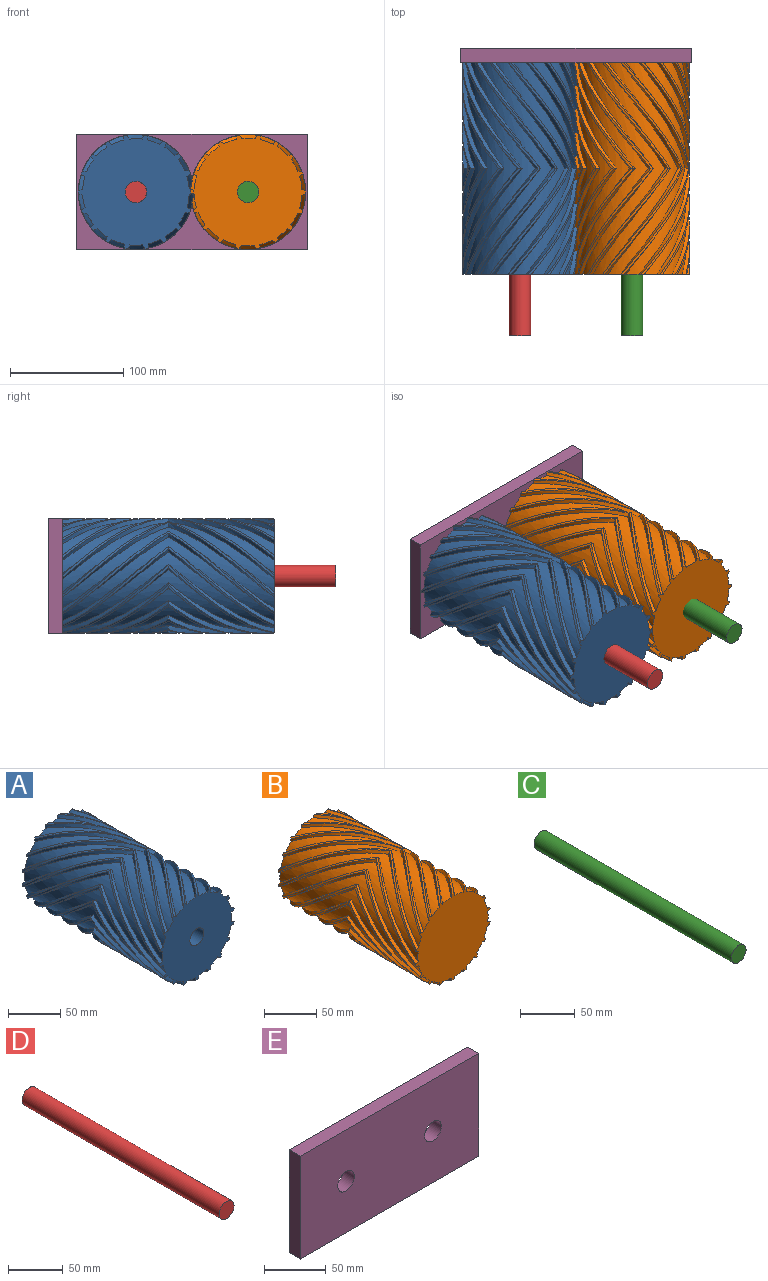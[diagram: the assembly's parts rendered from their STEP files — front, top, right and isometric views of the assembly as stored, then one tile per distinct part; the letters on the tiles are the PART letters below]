
ASSEMBLY  parts=5 mates=3
PART A: 129 faces, bbox 102.5x186.9x102.5 mm
  f0: plane 101.65x100.54mm, normal (0,-1,0), area 6946.6mm2, adj f1,f2,f3,f4,f5,f6,f7,f8
  f1: bspline ~93.47x69.89mm, area 471mm2, adj f0,f2,f4,f23
  f2: bspline ~93.47x71.15mm, area 235.9mm2, adj f0,f1,f3,f24
  f3: bspline ~93.47x68.96mm, area 471mm2, adj f0,f2,f16,f25
  f4: cylinder r=47.1mm len=186.94mm, axis (0,1,0), area 2157.7mm2, adj f0,f1,f22,f23,f97,f100
  f5: cylinder r=47.1mm len=186.94mm, axis (0,1,0), area 2157.7mm2, adj f0,f22,f31,f34,f35,f38
  f6: cylinder r=47.1mm len=186.94mm, axis (0,1,0), area 2157.7mm2, adj f0,f22,f37,f40,f41,f44
  f7: cylinder r=47.1mm len=186.94mm, axis (0,1,0), area 2157.7mm2, adj f0,f22,f43,f46,f47,f50
  f8: cylinder r=47.1mm len=186.94mm, axis (0,1,0), area 2157.7mm2, adj f0,f22,f49,f52,f53,f56
  f9: cylinder r=47.1mm len=186.94mm, axis (0,1,0), area 2157.7mm2, adj f0,f22,f55,f58,f59,f62
  f10: cylinder r=47.1mm len=186.94mm, axis (0,1,0), area 2157.7mm2, adj f0,f22,f61,f64,f65,f68
  f11: cylinder r=47.1mm len=186.94mm, axis (0,1,0), area 2157.7mm2, adj f0,f22,f67,f70,f77,f80
  f12: cylinder r=47.1mm len=186.94mm, axis (0,1,0), area 2157.7mm2, adj f0,f22,f73,f76,f89,f92
  f13: cylinder r=47.1mm len=186.94mm, axis (0,1,0), area 2157.7mm2, adj f0,f22,f71,f74,f79,f82
  f14: cylinder r=47.1mm len=186.94mm, axis (0,1,0), area 2157.7mm2, adj f0,f22,f85,f88,f95,f98
  f15: cylinder r=47.1mm len=186.94mm, axis (0,1,0), area 2157.7mm2, adj f0,f22,f83,f86,f91,f94
  f16: cylinder r=47.1mm len=186.94mm, axis (0,1,0), area 2157.7mm2, adj f0,f3,f22,f25,f26,f125
  f17: cylinder r=47.1mm len=186.94mm, axis (0,1,0), area 2157.7mm2, adj f0,f22,f103,f106,f113,f116
  f18: cylinder r=47.1mm len=186.94mm, axis (0,1,0), area 2157.7mm2, adj f0,f22,f29,f32,f109,f112
  f19: cylinder r=47.1mm len=186.94mm, axis (0,1,0), area 2157.7mm2, adj f0,f22,f115,f118,f119,f122
  f20: cylinder r=47.1mm len=186.94mm, axis (0,1,0), area 2157.7mm2, adj f0,f22,f107,f110,f121,f124
  f21: cylinder r=47.1mm len=186.94mm, axis (0,1,0), area 2157.7mm2, adj f0,f22,f28,f101,f104,f127
  f22: plane 101.65x100.54mm, normal (0,1,0), area 6946.6mm2, adj f4,f5,f6,f7,f8,f9,f10,f11
  f23: bspline ~93.47x69.89mm, area 471mm2, adj f1,f4,f22,f24
  f24: bspline ~93.47x71.15mm, area 235.9mm2, adj f2,f22,f23,f25
  f25: bspline ~93.47x68.96mm, area 471mm2, adj f3,f16,f22,f24
  f26: bspline ~93.47x60.41mm, area 471mm2, adj f16,f22,f27,f125
  f27: bspline ~93.47x60.34mm, area 235.9mm2, adj f22,f26,f28,f126
  f28: bspline ~93.47x57.85mm, area 471mm2, adj f21,f22,f27,f127
  f29: bspline ~93.47x53.27mm, area 471mm2, adj f18,f22,f30,f32
  f30: bspline ~93.47x52.25mm, area 235.9mm2, adj f22,f29,f31,f33
  f31: bspline ~93.47x53.27mm, area 471mm2, adj f5,f22,f30,f34
  f32: bspline ~93.47x53.27mm, area 471mm2, adj f0,f18,f29,f33
  f33: bspline ~93.47x52.25mm, area 235.9mm2, adj f0,f30,f32,f34
  f34: bspline ~93.47x53.27mm, area 471mm2, adj f0,f5,f31,f33
  f35: bspline ~93.47x64.39mm, area 471mm2, adj f0,f5,f36,f38
  f36: bspline ~93.47x66.76mm, area 235.9mm2, adj f0,f35,f37,f39
  f37: bspline ~93.47x66.03mm, area 471mm2, adj f0,f6,f36,f40
  f38: bspline ~93.47x64.39mm, area 471mm2, adj f5,f22,f35,f39
  f39: bspline ~93.47x66.76mm, area 235.9mm2, adj f22,f36,f38,f40
  f40: bspline ~93.47x66.03mm, area 471mm2, adj f6,f22,f37,f39
  f41: bspline ~93.47x71.45mm, area 471mm2, adj f0,f6,f42,f44
  f42: bspline ~93.47x73.38mm, area 235.9mm2, adj f0,f41,f43,f45
  f43: bspline ~93.47x71.76mm, area 471mm2, adj f0,f7,f42,f46
  f44: bspline ~93.47x71.45mm, area 471mm2, adj f6,f22,f41,f45
  f45: bspline ~93.47x73.38mm, area 235.9mm2, adj f22,f42,f44,f46
  f46: bspline ~93.47x71.76mm, area 471mm2, adj f7,f22,f43,f45
  f47: bspline ~93.47x69.89mm, area 471mm2, adj f0,f7,f48,f50
  f48: bspline ~93.47x71.15mm, area 235.9mm2, adj f0,f47,f49,f51
  f49: bspline ~93.47x68.96mm, area 471mm2, adj f0,f8,f48,f52
  f50: bspline ~93.47x69.89mm, area 471mm2, adj f7,f22,f47,f51
  f51: bspline ~93.47x71.15mm, area 235.9mm2, adj f22,f48,f50,f52
  f52: bspline ~93.47x68.96mm, area 471mm2, adj f8,f22,f49,f51
  f53: bspline ~93.47x60.41mm, area 471mm2, adj f0,f8,f54,f56
  f54: bspline ~93.47x60.34mm, area 235.9mm2, adj f0,f53,f55,f57
  f55: bspline ~93.47x57.85mm, area 471mm2, adj f0,f9,f54,f58
  f56: bspline ~93.47x60.41mm, area 471mm2, adj f8,f22,f53,f57
  f57: bspline ~93.47x60.34mm, area 235.9mm2, adj f22,f54,f56,f58
  f58: bspline ~93.47x57.85mm, area 471mm2, adj f9,f22,f55,f57
  f59: bspline ~93.47x57.85mm, area 471mm2, adj f0,f9,f60,f62
  f60: bspline ~93.47x60.34mm, area 235.9mm2, adj f0,f59,f61,f63
  f61: bspline ~93.47x60.41mm, area 471mm2, adj f0,f10,f60,f64
  f62: bspline ~93.47x57.85mm, area 471mm2, adj f9,f22,f59,f63
  f63: bspline ~93.47x60.34mm, area 235.9mm2, adj f22,f60,f62,f64
  f64: bspline ~93.47x60.41mm, area 471mm2, adj f10,f22,f61,f63
  f65: bspline ~93.47x68.96mm, area 471mm2, adj f0,f10,f66,f68
  f66: bspline ~93.47x71.15mm, area 235.9mm2, adj f0,f65,f67,f69
  f67: bspline ~93.47x69.89mm, area 471mm2, adj f0,f11,f66,f70
  f68: bspline ~93.47x68.96mm, area 471mm2, adj f10,f22,f65,f69
  f69: bspline ~93.47x71.15mm, area 235.9mm2, adj f22,f66,f68,f70
  f70: bspline ~93.47x69.89mm, area 471mm2, adj f11,f22,f67,f69
  f71: bspline ~93.47x66.03mm, area 471mm2, adj f0,f13,f72,f74
  f72: bspline ~93.47x66.76mm, area 235.9mm2, adj f0,f71,f73,f75
  f73: bspline ~93.47x64.39mm, area 471mm2, adj f0,f12,f72,f76
  f74: bspline ~93.47x66.03mm, area 471mm2, adj f13,f22,f71,f75
  f75: bspline ~93.47x66.76mm, area 235.9mm2, adj f22,f72,f74,f76
  f76: bspline ~93.47x64.39mm, area 471mm2, adj f12,f22,f73,f75
  f77: bspline ~93.47x71.76mm, area 471mm2, adj f0,f11,f78,f80
  f78: bspline ~93.47x73.38mm, area 235.9mm2, adj f0,f77,f79,f81
  f79: bspline ~93.47x71.45mm, area 471mm2, adj f0,f13,f78,f82
  f80: bspline ~93.47x71.76mm, area 471mm2, adj f11,f22,f77,f81
  f81: bspline ~93.47x73.38mm, area 235.9mm2, adj f22,f78,f80,f82
  f82: bspline ~93.47x71.45mm, area 471mm2, adj f13,f22,f79,f81
  f83: bspline ~93.47x64.39mm, area 471mm2, adj f0,f15,f84,f86
  f84: bspline ~93.47x66.76mm, area 235.9mm2, adj f0,f83,f85,f87
  f85: bspline ~93.47x66.03mm, area 471mm2, adj f0,f14,f84,f88
  f86: bspline ~93.47x64.39mm, area 471mm2, adj f15,f22,f83,f87
  f87: bspline ~93.47x66.76mm, area 235.9mm2, adj f22,f84,f86,f88
  f88: bspline ~93.47x66.03mm, area 471mm2, adj f14,f22,f85,f87
  f89: bspline ~93.47x53.27mm, area 471mm2, adj f0,f12,f90,f92
  f90: bspline ~93.47x52.25mm, area 235.9mm2, adj f0,f89,f91,f93
  f91: bspline ~93.47x53.27mm, area 471mm2, adj f0,f15,f90,f94
  f92: bspline ~93.47x53.27mm, area 471mm2, adj f12,f22,f89,f93
  f93: bspline ~93.47x52.25mm, area 235.9mm2, adj f22,f90,f92,f94
  f94: bspline ~93.47x53.27mm, area 471mm2, adj f15,f22,f91,f93
  f95: bspline ~93.47x71.45mm, area 471mm2, adj f0,f14,f96,f98
  f96: bspline ~93.47x73.38mm, area 235.9mm2, adj f0,f95,f97,f99
  f97: bspline ~93.47x71.76mm, area 471mm2, adj f0,f4,f96,f100
  f98: bspline ~93.47x71.45mm, area 471mm2, adj f14,f22,f95,f99
  f99: bspline ~93.47x73.38mm, area 235.9mm2, adj f22,f96,f98,f100
  f100: bspline ~93.47x71.76mm, area 471mm2, adj f4,f22,f97,f99
  f101: bspline ~93.47x57.85mm, area 471mm2, adj f21,f22,f102,f104
  f102: bspline ~93.47x60.34mm, area 235.9mm2, adj f22,f101,f103,f105
  f103: bspline ~93.47x60.41mm, area 471mm2, adj f17,f22,f102,f106
  f104: bspline ~93.47x57.85mm, area 471mm2, adj f0,f21,f101,f105
  f105: bspline ~93.47x60.34mm, area 235.9mm2, adj f0,f102,f104,f106
  f106: bspline ~93.47x60.41mm, area 471mm2, adj f0,f17,f103,f105
  f107: bspline ~93.47x66.03mm, area 471mm2, adj f20,f22,f108,f110
  f108: bspline ~93.47x66.76mm, area 235.9mm2, adj f22,f107,f109,f111
  f109: bspline ~93.47x64.39mm, area 471mm2, adj f18,f22,f108,f112
  f110: bspline ~93.47x66.03mm, area 471mm2, adj f0,f20,f107,f111
  f111: bspline ~93.47x66.76mm, area 235.9mm2, adj f0,f108,f110,f112
  f112: bspline ~93.47x64.39mm, area 471mm2, adj f0,f18,f109,f111
  f113: bspline ~93.47x68.96mm, area 471mm2, adj f17,f22,f114,f116
  f114: bspline ~93.47x71.15mm, area 235.9mm2, adj f22,f113,f115,f117
  f115: bspline ~93.47x69.89mm, area 471mm2, adj f19,f22,f114,f118
  f116: bspline ~93.47x68.96mm, area 471mm2, adj f0,f17,f113,f117
  f117: bspline ~93.47x71.15mm, area 235.9mm2, adj f0,f114,f116,f118
  f118: bspline ~93.47x69.89mm, area 471mm2, adj f0,f19,f115,f117
  f119: bspline ~93.47x71.76mm, area 471mm2, adj f19,f22,f120,f122
  f120: bspline ~93.47x73.38mm, area 235.9mm2, adj f22,f119,f121,f123
  f121: bspline ~93.47x71.45mm, area 471mm2, adj f20,f22,f120,f124
  f122: bspline ~93.47x71.76mm, area 471mm2, adj f0,f19,f119,f123
  f123: bspline ~93.47x73.38mm, area 235.9mm2, adj f0,f120,f122,f124
  f124: bspline ~93.47x71.45mm, area 471mm2, adj f0,f20,f121,f123
  f125: bspline ~93.47x60.41mm, area 471mm2, adj f0,f16,f26,f126
  f126: bspline ~93.47x60.34mm, area 235.9mm2, adj f0,f27,f125,f127
  f127: bspline ~93.47x57.85mm, area 471mm2, adj f0,f21,f28,f126
  f128: cylinder r=9.53mm len=186.94mm, axis (0,1,0), area 11188.1mm2, adj f0,f22
PART B: 128 faces, bbox 102.5x186.9x102.5 mm
  f0: plane 101.65x100.54mm, normal (0,-1,0), area 7343.5mm2, adj f1,f2,f3,f4,f5,f6,f7,f8
  f1: bspline ~93.47x69.89mm, area 406.7mm2, adj f0,f2,f4,f23
  f2: bspline ~93.47x71.15mm, area 235.9mm2, adj f0,f1,f3,f24
  f3: bspline ~93.47x68.96mm, area 406.7mm2, adj f0,f2,f16,f25
  f4: cylinder r=47.62mm len=186.94mm, axis (0,1,0), area 2227.2mm2, adj f0,f1,f22,f23,f97,f100
  f5: cylinder r=47.62mm len=186.94mm, axis (0,1,0), area 2227.2mm2, adj f0,f22,f31,f34,f35,f38
  f6: cylinder r=47.62mm len=186.94mm, axis (0,1,0), area 2227.2mm2, adj f0,f22,f37,f40,f41,f44
  f7: cylinder r=47.62mm len=186.94mm, axis (0,1,0), area 2227.2mm2, adj f0,f22,f43,f46,f47,f50
  f8: cylinder r=47.62mm len=186.94mm, axis (0,1,0), area 2227.2mm2, adj f0,f22,f49,f52,f53,f56
  f9: cylinder r=47.62mm len=186.94mm, axis (0,1,0), area 2227.2mm2, adj f0,f22,f55,f58,f59,f62
  f10: cylinder r=47.62mm len=186.94mm, axis (0,1,0), area 2227.2mm2, adj f0,f22,f61,f64,f65,f68
  f11: cylinder r=47.62mm len=186.94mm, axis (0,1,0), area 2227.2mm2, adj f0,f22,f67,f70,f77,f80
  f12: cylinder r=47.62mm len=186.94mm, axis (0,1,0), area 2227.2mm2, adj f0,f22,f73,f76,f89,f92
  f13: cylinder r=47.62mm len=186.94mm, axis (0,1,0), area 2227.2mm2, adj f0,f22,f71,f74,f79,f82
  f14: cylinder r=47.62mm len=186.94mm, axis (0,1,0), area 2227.2mm2, adj f0,f22,f85,f88,f95,f98
  f15: cylinder r=47.62mm len=186.94mm, axis (0,1,0), area 2227.2mm2, adj f0,f22,f83,f86,f91,f94
  f16: cylinder r=47.62mm len=186.94mm, axis (0,1,0), area 2227.2mm2, adj f0,f3,f22,f25,f26,f125
  f17: cylinder r=47.62mm len=186.94mm, axis (0,1,0), area 2227.2mm2, adj f0,f22,f103,f106,f113,f116
  f18: cylinder r=47.62mm len=186.94mm, axis (0,1,0), area 2227.2mm2, adj f0,f22,f29,f32,f109,f112
  f19: cylinder r=47.62mm len=186.94mm, axis (0,1,0), area 2227.2mm2, adj f0,f22,f115,f118,f119,f122
  f20: cylinder r=47.62mm len=186.94mm, axis (0,1,0), area 2227.2mm2, adj f0,f22,f107,f110,f121,f124
  f21: cylinder r=47.62mm len=186.94mm, axis (0,1,0), area 2227.2mm2, adj f0,f22,f28,f101,f104,f127
  f22: plane 101.65x100.54mm, normal (0,1,0), area 7343.5mm2, adj f4,f5,f6,f7,f8,f9,f10,f11
  f23: bspline ~93.47x69.89mm, area 406.7mm2, adj f1,f4,f22,f24
  f24: bspline ~93.47x71.15mm, area 235.9mm2, adj f2,f22,f23,f25
  f25: bspline ~93.47x68.96mm, area 406.7mm2, adj f3,f16,f22,f24
  f26: bspline ~93.47x60.41mm, area 406.7mm2, adj f16,f22,f27,f125
  f27: bspline ~93.47x60.34mm, area 235.9mm2, adj f22,f26,f28,f126
  f28: bspline ~93.47x57.85mm, area 406.7mm2, adj f21,f22,f27,f127
  f29: bspline ~93.47x53.18mm, area 406.7mm2, adj f18,f22,f30,f32
  f30: bspline ~93.47x52.25mm, area 235.9mm2, adj f22,f29,f31,f33
  f31: bspline ~93.47x53.18mm, area 406.7mm2, adj f5,f22,f30,f34
  f32: bspline ~93.47x53.18mm, area 406.7mm2, adj f0,f18,f29,f33
  f33: bspline ~93.47x52.25mm, area 235.9mm2, adj f0,f30,f32,f34
  f34: bspline ~93.47x53.18mm, area 406.7mm2, adj f0,f5,f31,f33
  f35: bspline ~93.47x64.39mm, area 406.7mm2, adj f0,f5,f36,f38
  f36: bspline ~93.47x66.76mm, area 235.9mm2, adj f0,f35,f37,f39
  f37: bspline ~93.47x66.02mm, area 406.7mm2, adj f0,f6,f36,f40
  f38: bspline ~93.47x64.39mm, area 406.7mm2, adj f5,f22,f35,f39
  f39: bspline ~93.47x66.76mm, area 235.9mm2, adj f22,f36,f38,f40
  f40: bspline ~93.47x66.02mm, area 406.7mm2, adj f6,f22,f37,f39
  f41: bspline ~93.47x71.45mm, area 406.7mm2, adj f0,f6,f42,f44
  f42: bspline ~93.47x73.38mm, area 235.9mm2, adj f0,f41,f43,f45
  f43: bspline ~93.47x71.76mm, area 406.7mm2, adj f0,f7,f42,f46
  f44: bspline ~93.47x71.45mm, area 406.7mm2, adj f6,f22,f41,f45
  f45: bspline ~93.47x73.38mm, area 235.9mm2, adj f22,f42,f44,f46
  f46: bspline ~93.47x71.76mm, area 406.7mm2, adj f7,f22,f43,f45
  f47: bspline ~93.47x69.89mm, area 406.7mm2, adj f0,f7,f48,f50
  f48: bspline ~93.47x71.15mm, area 235.9mm2, adj f0,f47,f49,f51
  f49: bspline ~93.47x68.96mm, area 406.7mm2, adj f0,f8,f48,f52
  f50: bspline ~93.47x69.89mm, area 406.7mm2, adj f7,f22,f47,f51
  f51: bspline ~93.47x71.15mm, area 235.9mm2, adj f22,f48,f50,f52
  f52: bspline ~93.47x68.96mm, area 406.7mm2, adj f8,f22,f49,f51
  f53: bspline ~93.47x60.41mm, area 406.7mm2, adj f0,f8,f54,f56
  f54: bspline ~93.47x60.34mm, area 235.9mm2, adj f0,f53,f55,f57
  f55: bspline ~93.47x57.85mm, area 406.7mm2, adj f0,f9,f54,f58
  f56: bspline ~93.47x60.41mm, area 406.7mm2, adj f8,f22,f53,f57
  f57: bspline ~93.47x60.34mm, area 235.9mm2, adj f22,f54,f56,f58
  f58: bspline ~93.47x57.85mm, area 406.7mm2, adj f9,f22,f55,f57
  f59: bspline ~93.47x57.85mm, area 406.7mm2, adj f0,f9,f60,f62
  f60: bspline ~93.47x60.34mm, area 235.9mm2, adj f0,f59,f61,f63
  f61: bspline ~93.47x60.41mm, area 406.7mm2, adj f0,f10,f60,f64
  f62: bspline ~93.47x57.85mm, area 406.7mm2, adj f9,f22,f59,f63
  f63: bspline ~93.47x60.34mm, area 235.9mm2, adj f22,f60,f62,f64
  f64: bspline ~93.47x60.41mm, area 406.7mm2, adj f10,f22,f61,f63
  f65: bspline ~93.47x68.96mm, area 406.7mm2, adj f0,f10,f66,f68
  f66: bspline ~93.47x71.15mm, area 235.9mm2, adj f0,f65,f67,f69
  f67: bspline ~93.47x69.89mm, area 406.7mm2, adj f0,f11,f66,f70
  f68: bspline ~93.47x68.96mm, area 406.7mm2, adj f10,f22,f65,f69
  f69: bspline ~93.47x71.15mm, area 235.9mm2, adj f22,f66,f68,f70
  f70: bspline ~93.47x69.89mm, area 406.7mm2, adj f11,f22,f67,f69
  f71: bspline ~93.47x66.02mm, area 406.7mm2, adj f0,f13,f72,f74
  f72: bspline ~93.47x66.76mm, area 235.9mm2, adj f0,f71,f73,f75
  f73: bspline ~93.47x64.39mm, area 406.7mm2, adj f0,f12,f72,f76
  f74: bspline ~93.47x66.02mm, area 406.7mm2, adj f13,f22,f71,f75
  f75: bspline ~93.47x66.76mm, area 235.9mm2, adj f22,f72,f74,f76
  f76: bspline ~93.47x64.39mm, area 406.7mm2, adj f12,f22,f73,f75
  f77: bspline ~93.47x71.76mm, area 406.7mm2, adj f0,f11,f78,f80
  f78: bspline ~93.47x73.38mm, area 235.9mm2, adj f0,f77,f79,f81
  f79: bspline ~93.47x71.45mm, area 406.7mm2, adj f0,f13,f78,f82
  f80: bspline ~93.47x71.76mm, area 406.7mm2, adj f11,f22,f77,f81
  f81: bspline ~93.47x73.38mm, area 235.9mm2, adj f22,f78,f80,f82
  f82: bspline ~93.47x71.45mm, area 406.7mm2, adj f13,f22,f79,f81
  f83: bspline ~93.47x64.39mm, area 406.7mm2, adj f0,f15,f84,f86
  f84: bspline ~93.47x66.76mm, area 235.9mm2, adj f0,f83,f85,f87
  f85: bspline ~93.47x66.02mm, area 406.7mm2, adj f0,f14,f84,f88
  f86: bspline ~93.47x64.39mm, area 406.7mm2, adj f15,f22,f83,f87
  f87: bspline ~93.47x66.76mm, area 235.9mm2, adj f22,f84,f86,f88
  f88: bspline ~93.47x66.02mm, area 406.7mm2, adj f14,f22,f85,f87
  f89: bspline ~93.47x53.18mm, area 406.7mm2, adj f0,f12,f90,f92
  f90: bspline ~93.47x52.25mm, area 235.9mm2, adj f0,f89,f91,f93
  f91: bspline ~93.47x53.18mm, area 406.7mm2, adj f0,f15,f90,f94
  f92: bspline ~93.47x53.18mm, area 406.7mm2, adj f12,f22,f89,f93
  f93: bspline ~93.47x52.25mm, area 235.9mm2, adj f22,f90,f92,f94
  f94: bspline ~93.47x53.18mm, area 406.7mm2, adj f15,f22,f91,f93
  f95: bspline ~93.47x71.45mm, area 406.7mm2, adj f0,f14,f96,f98
  f96: bspline ~93.47x73.38mm, area 235.9mm2, adj f0,f95,f97,f99
  f97: bspline ~93.47x71.76mm, area 406.7mm2, adj f0,f4,f96,f100
  f98: bspline ~93.47x71.45mm, area 406.7mm2, adj f14,f22,f95,f99
  f99: bspline ~93.47x73.38mm, area 235.9mm2, adj f22,f96,f98,f100
  f100: bspline ~93.47x71.76mm, area 406.7mm2, adj f4,f22,f97,f99
  f101: bspline ~93.47x57.85mm, area 406.7mm2, adj f21,f22,f102,f104
  f102: bspline ~93.47x60.34mm, area 235.9mm2, adj f22,f101,f103,f105
  f103: bspline ~93.47x60.41mm, area 406.7mm2, adj f17,f22,f102,f106
  f104: bspline ~93.47x57.85mm, area 406.7mm2, adj f0,f21,f101,f105
  f105: bspline ~93.47x60.34mm, area 235.9mm2, adj f0,f102,f104,f106
  f106: bspline ~93.47x60.41mm, area 406.7mm2, adj f0,f17,f103,f105
  f107: bspline ~93.47x66.02mm, area 406.7mm2, adj f20,f22,f108,f110
  f108: bspline ~93.47x66.76mm, area 235.9mm2, adj f22,f107,f109,f111
  f109: bspline ~93.47x64.39mm, area 406.7mm2, adj f18,f22,f108,f112
  f110: bspline ~93.47x66.02mm, area 406.7mm2, adj f0,f20,f107,f111
  f111: bspline ~93.47x66.76mm, area 235.9mm2, adj f0,f108,f110,f112
  f112: bspline ~93.47x64.39mm, area 406.7mm2, adj f0,f18,f109,f111
  f113: bspline ~93.47x68.96mm, area 406.7mm2, adj f17,f22,f114,f116
  f114: bspline ~93.47x71.15mm, area 235.9mm2, adj f22,f113,f115,f117
  f115: bspline ~93.47x69.89mm, area 406.7mm2, adj f19,f22,f114,f118
  f116: bspline ~93.47x68.96mm, area 406.7mm2, adj f0,f17,f113,f117
  f117: bspline ~93.47x71.15mm, area 235.9mm2, adj f0,f114,f116,f118
  f118: bspline ~93.47x69.89mm, area 406.7mm2, adj f0,f19,f115,f117
  f119: bspline ~93.47x71.76mm, area 406.7mm2, adj f19,f22,f120,f122
  f120: bspline ~93.47x73.38mm, area 235.9mm2, adj f22,f119,f121,f123
  f121: bspline ~93.47x71.45mm, area 406.7mm2, adj f20,f22,f120,f124
  f122: bspline ~93.47x71.76mm, area 406.7mm2, adj f0,f19,f119,f123
  f123: bspline ~93.47x73.38mm, area 235.9mm2, adj f0,f120,f122,f124
  f124: bspline ~93.47x71.45mm, area 406.7mm2, adj f0,f20,f121,f123
  f125: bspline ~93.47x60.41mm, area 406.7mm2, adj f0,f16,f26,f126
  f126: bspline ~93.47x60.34mm, area 235.9mm2, adj f0,f27,f125,f127
  f127: bspline ~93.47x57.85mm, area 406.7mm2, adj f0,f21,f28,f126
PART C: 3 faces, bbox 19.1x254x19.1 mm
  f0: cylinder r=9.53mm len=254mm, axis (0,1,0), area 15201.2mm2, adj f1,f2
  f1: plane 19.05x19.05mm, normal (0,-1,0), area 285mm2, adj f0
  f2: plane 19.05x19.05mm, normal (0,1,0), area 285mm2, adj f0
PART D: 3 faces, bbox 19.1x254x19.1 mm
  f0: cylinder r=9.53mm len=254mm, axis (0,1,0), area 15201.2mm2, adj f1,f2
  f1: plane 19.05x19.05mm, normal (0,-1,0), area 285mm2, adj f0
  f2: plane 19.05x19.05mm, normal (0,1,0), area 285mm2, adj f0
PART E: 8 faces, bbox 203.2x12.7x101.6 mm
  f0: plane 101.6x12.7mm, normal (-1,0,0), area 1290.3mm2, adj f1,f4,f6,f7
  f1: plane 203.2x12.7mm, normal (0,0,-1), area 2580.6mm2, adj f0,f2,f6,f7
  f2: plane 101.6x12.7mm, normal (1,0,0), area 1290.3mm2, adj f1,f4,f6,f7
  f3: cylinder r=9.53mm len=19.05mm, axis (0,-1,0), area 760.1mm2, adj f6,f7
  f4: plane 203.2x12.7mm, normal (0,0,1), area 2580.6mm2, adj f0,f2,f6,f7
  f5: cylinder r=9.53mm len=19.05mm, axis (0,-1,0), area 760.1mm2, adj f6,f7
  f6: plane 203.2x101.6mm, normal (0,1,0), area 20075.1mm2, adj f0,f1,f2,f3,f4,f5
  f7: plane 203.2x101.6mm, normal (0,-1,0), area 20075.1mm2, adj f0,f1,f2,f3,f4,f5
PLACE A rot(axis=(0,-1,0),30.4deg) t=(136.91,27.84,20.51)mm
PLACE B rot(axis=(0,1,0),30.4deg) t=(235.97,27.84,20.51)mm
PLACE C t=(186.44,134.02,20.51)mm
PLACE D t=(186.44,134.02,20.51)mm
PLACE E t=(186.44,121.32,20.51)mm fixed
MATE revolute A.f4 <-> E.f3  axis (0,1,0) through (136.91,121.32,20.51)mm
MATE fastened C.f0 <-> E.f5  axis (0,1,0) through (235.97,134.02,20.51)mm
MATE revolute B.f4 <-> E.f5  axis (0,1,0) through (235.97,121.32,20.51)mm
